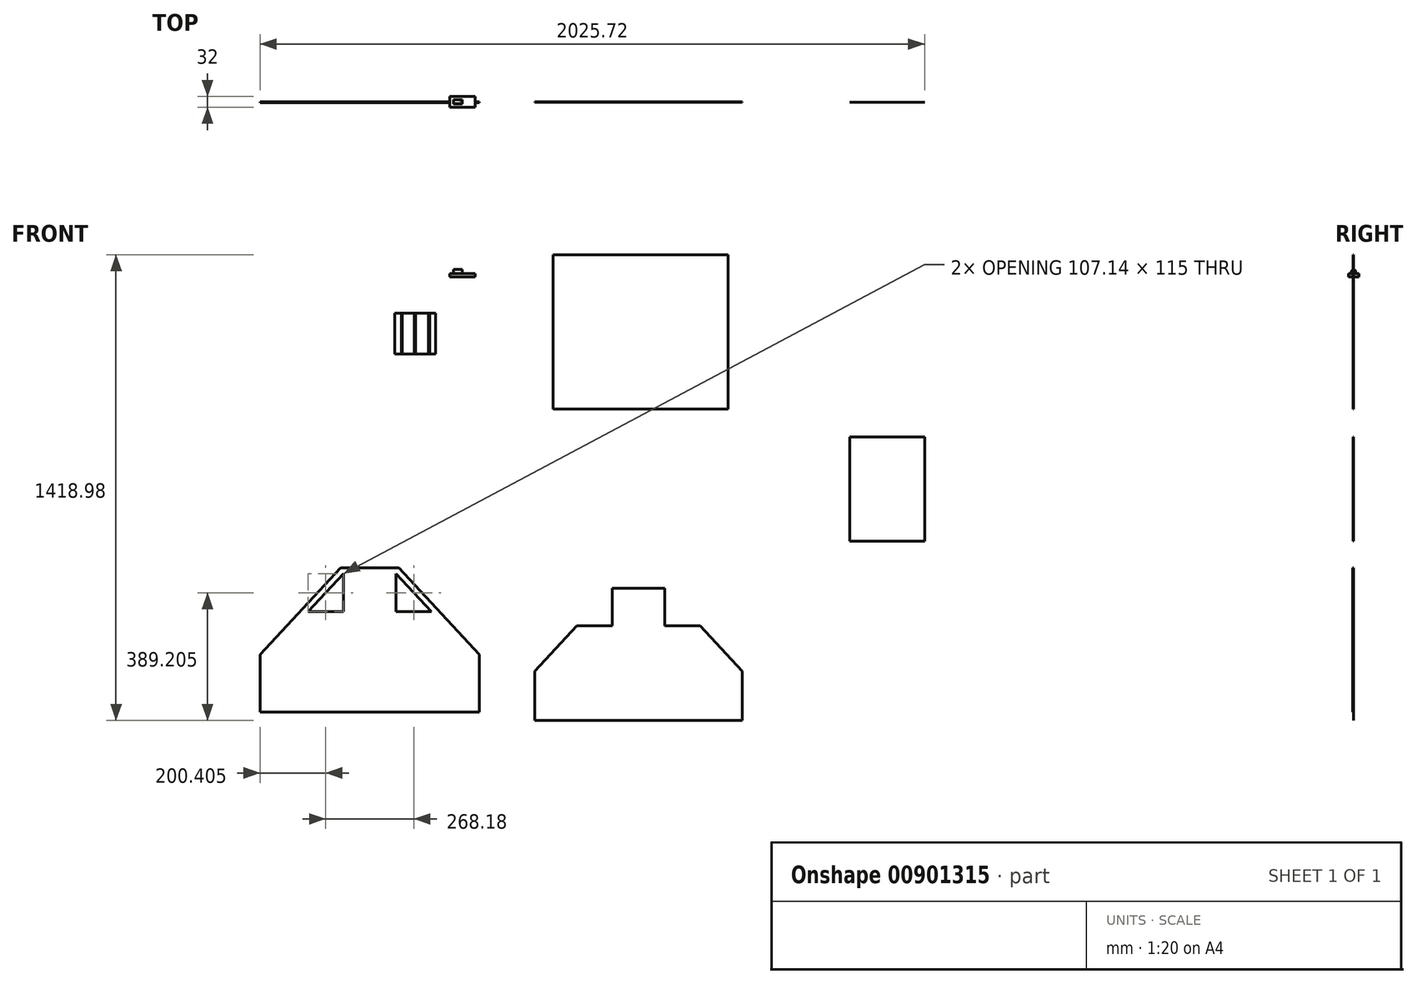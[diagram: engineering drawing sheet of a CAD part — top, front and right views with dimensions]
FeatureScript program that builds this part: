
annotation { "Feature Type Name" : "Feature", "Feature Type Description" : "" }
export const myFeature = defineFeature(function(context is Context, id is Id, definition is map)
    precondition{}
    {
        {
            var Q0;
            Q0=qCreatedBy(makeId("Front.planeOp"),FACE);
            var sketch = newSketch(context, id + "F0", { "sketchPlane" : qUnion([Q0])});
            skLineSegment(sketch, "E0.bottom", {"start": v(751.3, 665.77) * mm, "end": v(876.3, 665.77) * mm});
            skLineSegment(sketch, "E0.top", {"start": v(751.3, 540.77) * mm, "end": v(876.3, 540.77) * mm});
            skLineSegment(sketch, "E0.left", {"start": v(751.3, 665.77) * mm, "end": v(751.3, 540.77) * mm});
            skLineSegment(sketch, "E0.right", {"start": v(876.3, 665.77) * mm, "end": v(876.3, 540.77) * mm});
            skPoint(sketch, "E1.visualSharp", {"position": v(751.3, 665.77) * mm});
            skLineSegment(sketch, "E1.filletArc", {"start": v(751.3, 665.77) * mm, "end": v(751.3, 665.77) * mm});
            skPoint(sketch, "E2.visualSharp", {"position": v(876.3, 665.77) * mm});
            skLineSegment(sketch, "E2.filletArc", {"start": v(876.3, 665.77) * mm, "end": v(876.3, 665.77) * mm});
            skPoint(sketch, "E3.visualSharp", {"position": v(876.3, 540.77) * mm});
            skLineSegment(sketch, "E3.filletArc", {"start": v(876.3, 540.77) * mm, "end": v(876.3, 540.77) * mm});
            skPoint(sketch, "E4.visualSharp", {"position": v(751.3, 540.77) * mm});
            skLineSegment(sketch, "E4.filletArc", {"start": v(751.3, 540.77) * mm, "end": v(751.3, 540.77) * mm});
            skLineSegment(sketch, "E5.bottom", {"start": v(3038.85, 81858.35) * mm, "end": v(2869.38, 81858.35) * mm});
            skLineSegment(sketch, "E5.top", {"start": v(3038.85, 72650.5) * mm, "end": v(2869.38, 72650.5) * mm});
            skLineSegment(sketch, "E5.left", {"start": v(3038.85, 81858.35) * mm, "end": v(3038.85, 72650.5) * mm});
            skLineSegment(sketch, "E5.right", {"start": v(2869.38, 81858.35) * mm, "end": v(2869.38, 72650.5) * mm});
            skSolve(sketch);
        }
        {
            var Q0;
            Q0=makeQuery(id+"F0.imprint","IMPRINT",FACE,{"disambiguationData":[TD([[makeQuery(id+"F0.imprint","IMPRINT",EDGE,{"derivedFrom":sQuery(id+"F0.wireOp",EDGE,"E0.bottom")}),-1.0]])]});
            extrude(context, id + "F1", {"entities" : qUnion([Q0]), "depth" : 1 * mm, "offsetDistance" : 25 * mm});
        }
        {
            var Q0;
            Q0=makeQuery(id+"F1.opExtrude","CAP_FACE",FACE,{"disambiguationData":[OSD([sQuery(id+"F0.wireOp",EDGE,"E0.bottom"),sQuery(id+"F0.wireOp",EDGE,"E0.top"),sQuery(id+"F0.wireOp",EDGE,"E0.left"),sQuery(id+"F0.wireOp",EDGE,"E0.right"),sQuery(id+"F0.wireOp",EDGE,"E1.filletArc"),sQuery(id+"F0.wireOp",EDGE,"E2.filletArc"),sQuery(id+"F0.wireOp",EDGE,"E3.filletArc"),sQuery(id+"F0.wireOp",EDGE,"E4.filletArc")])],"isStart":false});
            var sketch = newSketch(context, id + "F2", { "sketchPlane" : qUnion([Q0])});
            skLineSegment(sketch, "E6.bottom", {"start": v(1062.52, 675.31) * mm, "end": v(1065.96, 675.31) * mm});
            skLineSegment(sketch, "E6.top", {"start": v(1062.52, 550.31) * mm, "end": v(1065.96, 550.31) * mm});
            skLineSegment(sketch, "E6.left", {"start": v(1062.52, 675.31) * mm, "end": v(1062.52, 550.31) * mm});
            skLineSegment(sketch, "E6.right", {"start": v(1065.96, 675.31) * mm, "end": v(1065.96, 550.31) * mm});
            skLineSegment(sketch, "E7.bottom", {"start": v(1040.06, 681.56) * mm, "end": v(1043.5, 681.56) * mm});
            skLineSegment(sketch, "E7.top", {"start": v(1040.06, 556.56) * mm, "end": v(1043.5, 556.56) * mm});
            skLineSegment(sketch, "E7.left", {"start": v(1040.06, 681.56) * mm, "end": v(1040.06, 556.56) * mm});
            skLineSegment(sketch, "E7.right", {"start": v(1043.5, 681.56) * mm, "end": v(1043.5, 556.56) * mm});
            skLineSegment(sketch, "E8.bottom", {"start": v(1006.11, 664.93) * mm, "end": v(1009.55, 664.93) * mm});
            skLineSegment(sketch, "E8.top", {"start": v(1006.11, 539.93) * mm, "end": v(1009.55, 539.93) * mm});
            skLineSegment(sketch, "E8.left", {"start": v(1006.11, 664.93) * mm, "end": v(1006.11, 539.93) * mm});
            skLineSegment(sketch, "E8.right", {"start": v(1009.55, 664.93) * mm, "end": v(1009.55, 539.93) * mm});
            skPoint(sketch, "E9.firstSnap0", {"position": v(1043.5, 619.06) * mm});
            skPoint(sketch, "E9.oppositeSnap0", {"position": v(1043.5, 619.06) * mm});
            skSolve(sketch);
        }
        {
            var Q0;
            Q0=makeQuery(id+"F2.imprint","IMPRINT",FACE,{"disambiguationData":[TD([[makeQuery(id+"F2.imprint","IMPRINT",EDGE,{"derivedFrom":sQuery(id+"F2.wireOp",EDGE,"E6.bottom")}),-1.0]])]});
            var Q1;
            Q1=makeQuery(id+"F2.imprint","IMPRINT",FACE,{"disambiguationData":[TD([[makeQuery(id+"F2.imprint","IMPRINT",EDGE,{"derivedFrom":sQuery(id+"F2.wireOp",EDGE,"E7.bottom")}),-1.0]])]});
            var Q2;
            Q2=makeQuery(id+"F2.imprint","IMPRINT",FACE,{"disambiguationData":[TD([[makeQuery(id+"F2.imprint","IMPRINT",EDGE,{"derivedFrom":sQuery(id+"F2.wireOp",EDGE,"E8.bottom")}),-1.0]])]});
            extrude(context, id + "F3", {"entities" : qUnion([Q0, Q1, Q2]), "depth" : 0.1 * mm, "offsetDistance" : 25 * mm});
        }
        {
            var Q0;
            Q0=makeQuery(id+"F3.opExtrude","SWEPT_BODY",BODY,{"disambiguationData":[OSD([sQuery(id+"F2.wireOp",EDGE,"E8.bottom"),sQuery(id+"F2.wireOp",EDGE,"E8.top"),sQuery(id+"F2.wireOp",EDGE,"E8.left"),sQuery(id+"F2.wireOp",EDGE,"E8.right")])]});
            transform(context, id + "F4", {"entities" : qUnion([Q0]), "transformType" : TransformType.TRANSLATION_3D, "dx" : -232.8 * mm, "dy" : 0 * mm, "dz" : 3.3 * mm, "makeCopy" : false});
        }
        {
            var Q0;
            Q0=makeQuery(id+"F3.opExtrude","SWEPT_BODY",BODY,{"disambiguationData":[OSD([sQuery(id+"F2.wireOp",EDGE,"E8.bottom"),sQuery(id+"F2.wireOp",EDGE,"E8.top"),sQuery(id+"F2.wireOp",EDGE,"E8.left"),sQuery(id+"F2.wireOp",EDGE,"E8.right")])]});
            transform(context, id + "F5", {"entities" : qUnion([Q0]), "transformType" : TransformType.TRANSLATION_3D, "dx" : 6E-4000 * mm, "dy" : 0 * mm, "dz" : 0 * mm, "makeCopy" : false});
        }
        {
            var Q0;
            Q0=makeQuery(id+"F3.opExtrude","SWEPT_BODY",BODY,{"disambiguationData":[OSD([sQuery(id+"F2.wireOp",EDGE,"E8.bottom"),sQuery(id+"F2.wireOp",EDGE,"E8.top"),sQuery(id+"F2.wireOp",EDGE,"E8.left"),sQuery(id+"F2.wireOp",EDGE,"E8.right")])]});
            var Q1;
            Q1=makeQuery(id+"F3.opExtrude","CAP_VERTEX",VERTEX,{"disambiguationData":[OSD([sQuery(id+"F2.wireOp",EDGE,"E8.top"),sQuery(id+"F2.wireOp",EDGE,"E8.left")])],"isStart":false});
            var Q2;
            Q2=makeQuery(id+"F1.opExtrude","CAP_EDGE",EDGE,{"disambiguationData":[OSD([sQuery(id+"F0.wireOp",EDGE,"E0.top")])],"isStart":false});
            transform(context, id + "F6", {"entities" : qUnion([Q0]), "transformType" : TransformType.TRANSLATION_ENTITY, "oppositeDirectionEntity" : false, "transformLine" : qUnion([Q1, Q2]), "makeCopy" : false});
        }
        {
            var Q0;
            Q0=makeQuery(id+"F3.opExtrude","SWEPT_BODY",BODY,{"disambiguationData":[OSD([sQuery(id+"F2.wireOp",EDGE,"E8.bottom"),sQuery(id+"F2.wireOp",EDGE,"E8.top"),sQuery(id+"F2.wireOp",EDGE,"E8.left"),sQuery(id+"F2.wireOp",EDGE,"E8.right")])]});
            var Q1;
            Q1=makeQuery(id+"F3.opExtrude","CAP_VERTEX",VERTEX,{"disambiguationData":[OSD([sQuery(id+"F2.wireOp",EDGE,"E8.bottom"),sQuery(id+"F2.wireOp",EDGE,"E8.right")])],"isStart":true});
            var Q2;
            Q2=makeQuery(id+"F1.opExtrude","CAP_VERTEX",VERTEX,{"disambiguationData":[OSD([sQuery(id+"F0.wireOp",EDGE,"E0.bottom"),sQuery(id+"F0.wireOp",EDGE,"E2.filletArc")])],"isStart":false});
            transform(context, id + "F7", {"entities" : qUnion([Q0]), "transformType" : TransformType.TRANSLATION_ENTITY, "oppositeDirectionEntity" : false, "transformLine" : qUnion([Q1, Q2]), "makeCopy" : false});
        }
        {
            var Q0;
            Q0=makeQuery(id+"F3.opExtrude","SWEPT_BODY",BODY,{"disambiguationData":[OSD([sQuery(id+"F2.wireOp",EDGE,"E7.bottom"),sQuery(id+"F2.wireOp",EDGE,"E7.top"),sQuery(id+"F2.wireOp",EDGE,"E7.left"),sQuery(id+"F2.wireOp",EDGE,"E7.right")])]});
            var Q1;
            Q1=sQuery(id+"F2.wireOp",VERTEX,"E7.bottom.start");
            var Q2;
            Q2=makeQuery(id+"F1.opExtrude","CAP_VERTEX",VERTEX,{"disambiguationData":[OSD([sQuery(id+"F0.wireOp",EDGE,"E0.bottom"),sQuery(id+"F0.wireOp",EDGE,"E1.filletArc")])],"isStart":false});
            transform(context, id + "F8", {"entities" : qUnion([Q0]), "transformType" : TransformType.TRANSLATION_ENTITY, "oppositeDirectionEntity" : false, "transformLine" : qUnion([Q1, Q2]), "makeCopy" : false});
        }
        {
            var Q0;
            Q0=sQuery(id+"F2.wireOp",EDGE,"E6.bottom");
            cPoint(context, id + "F9", {"entities" : qUnion([Q0]), "parameter" : 0.5});
        }
        {
            var Q0;
            Q0=makeQuery(id+"F1.opExtrude","CAP_EDGE",EDGE,{"disambiguationData":[OSD([sQuery(id+"F0.wireOp",EDGE,"E0.bottom")])],"isStart":false});
            cPoint(context, id + "F10", {"entities" : qUnion([Q0]), "parameter" : 0.5});
        }
        {
            var Q0;
            Q0=makeQuery(id+"F3.opExtrude","SWEPT_BODY",BODY,{"disambiguationData":[OSD([sQuery(id+"F2.wireOp",EDGE,"E6.bottom"),sQuery(id+"F2.wireOp",EDGE,"E6.top"),sQuery(id+"F2.wireOp",EDGE,"E6.left"),sQuery(id+"F2.wireOp",EDGE,"E6.right")])]});
            var Q1;
            Q1=qCreatedBy(id+"F9",VERTEX);
            var Q2;
            Q2=qCreatedBy(id+"F10",VERTEX);
            transform(context, id + "F11", {"entities" : qUnion([Q0]), "transformType" : TransformType.TRANSLATION_ENTITY, "oppositeDirectionEntity" : false, "transformLine" : qUnion([Q1, Q2]), "makeCopy" : false});
        }
        {
            var Q0;
            Q0=qCreatedBy(makeId("Front.planeOp"),FACE);
            var sketch = newSketch(context, id + "F12", { "sketchPlane" : qUnion([Q0])});
            skLineSegment(sketch, "E10.bottom", {"start": v(919.16, 786.05) * mm, "end": v(997.16, 786.05) * mm});
            skLineSegment(sketch, "E10.top", {"start": v(919.16, 776.05) * mm, "end": v(997.16, 776.05) * mm});
            skLineSegment(sketch, "E10.left", {"start": v(919.16, 786.05) * mm, "end": v(919.16, 776.05) * mm});
            skLineSegment(sketch, "E10.right", {"start": v(997.16, 786.05) * mm, "end": v(997.16, 776.05) * mm});
            skPoint(sketch, "E11.oppositeSnap0", {"position": v(958.16, 786.05) * mm});
            skLineSegment(sketch, "E11.bottom", {"start": v(997.16, 786.05) * mm, "end": v(958.16, 786.05) * mm});
            skLineSegment(sketch, "E11.top", {"start": v(997.16, 798.75) * mm, "end": v(958.16, 798.75) * mm});
            skLineSegment(sketch, "E11.left", {"start": v(997.16, 786.05) * mm, "end": v(997.16, 798.75) * mm});
            skLineSegment(sketch, "E11.right", {"start": v(958.16, 786.05) * mm, "end": v(958.16, 798.75) * mm});
            skLineSegment(sketch, "E12.bottom", {"start": v(958.16, 792.4) * mm, "end": v(930.77, 792.4) * mm});
            skLineSegment(sketch, "E12.top", {"start": v(958.16, 786.05) * mm, "end": v(930.77, 786.05) * mm});
            skLineSegment(sketch, "E12.left", {"start": v(958.16, 792.4) * mm, "end": v(958.16, 786.05) * mm});
            skLineSegment(sketch, "E12.right", {"start": v(930.77, 792.4) * mm, "end": v(930.77, 786.05) * mm});
            skSolve(sketch);
        }
        {
            var Q0;
            Q0=makeQuery(id+"F12.imprint","IMPRINT",FACE,{"disambiguationData":[TD([[makeQuery(id+"F12.imprint","IMPRINT",EDGE,{"derivedFrom":sQuery(id+"F12.wireOp",EDGE,"E11.bottom")}),-1.0]])]});
            var Q1;
            Q1=makeQuery(id+"F12.imprint","IMPRINT",FACE,{"disambiguationData":[TD([[makeQuery(id+"F12.imprint","IMPRINT",EDGE,{"derivedFrom":sQuery(id+"F12.wireOp",EDGE,"E10.bottom")}),-1.0]])]});
            extrude(context, id + "F13", {"entities" : qUnion([Q0, Q1]), "endBound" : BoundingType.SYMMETRIC, "depth" : 32 * mm, "offsetDistance" : 25 * mm});
        }
        {
            var Q0;
            Q0=makeQuery(id+"F12.imprint","IMPRINT",FACE,{"disambiguationData":[TD([[makeQuery(id+"F12.imprint","IMPRINT",EDGE,{"derivedFrom":sQuery(id+"F12.wireOp",EDGE,"E12.bottom")}),1.0]])]});
            var Q1;
            Q1=sQuery(id+"F12.wireOp",EDGE,"E12.bottom");
            revolve(context, id + "F14", {"surfaceOperationType" : NewSurfaceOperationType.NEW, "entities" : qUnion([Q0]), "axis" : qUnion([Q1]), "revolveType" : RevolveType.ONE_DIRECTION, "angle" : 360 * degree});
        }
        {
            var Q0;
            Q0=makeQuery(id+"F14.opRevolve","SWEPT_FACE",FACE,{"disambiguationData":[OSD([sQuery(id+"F12.wireOp",EDGE,"E12.right")])]});
            var sketch = newSketch(context, id + "F15", { "sketchPlane" : qUnion([Q0])});
            skCircle(sketch, "E13", {"center": v(0, 792.4) * mm, "radius": 7.66 * mm});
            skSolve(sketch);
        }
        {
            var Q0;
            Q0=makeQuery(id+"F15.imprint","IMPRINT",FACE,{"disambiguationData":[TD([[makeQuery(id+"F15.imprint","IMPRINT",EDGE,{"derivedFrom":sQuery(id+"F15.wireOp",EDGE,"E13")}),1.0]])]});
            extrude(context, id + "F16", {"entities" : qUnion([Q0]), "operationType" : NewBodyOperationType.REMOVE, "depth" : -20 * mm, "offsetDistance" : 25 * mm});
        }
        {
            var Q0;
            Q0=makeQuery(id+"F1.opExtrude","CAP_FACE",FACE,{"disambiguationData":[OSD([sQuery(id+"F0.wireOp",EDGE,"E0.bottom"),sQuery(id+"F0.wireOp",EDGE,"E0.top"),sQuery(id+"F0.wireOp",EDGE,"E0.left"),sQuery(id+"F0.wireOp",EDGE,"E0.right"),sQuery(id+"F0.wireOp",EDGE,"E1.filletArc"),sQuery(id+"F0.wireOp",EDGE,"E2.filletArc"),sQuery(id+"F0.wireOp",EDGE,"E3.filletArc"),sQuery(id+"F0.wireOp",EDGE,"E4.filletArc")])],"isStart":false});
            var sketch = newSketch(context, id + "F17", { "sketchPlane" : qUnion([Q0])});
            skLineSegment(sketch, "E14.bottom", {"start": v(1234.72, 843.78) * mm, "end": v(1768.12, 843.78) * mm});
            skLineSegment(sketch, "E14.top", {"start": v(1234.72, 373.88) * mm, "end": v(1768.12, 373.88) * mm});
            skLineSegment(sketch, "E14.left", {"start": v(1234.72, 843.78) * mm, "end": v(1234.72, 373.88) * mm});
            skLineSegment(sketch, "E14.right", {"start": v(1768.12, 843.78) * mm, "end": v(1768.12, 373.88) * mm});
            skSolve(sketch);
        }
        {
            var Q0;
            Q0=makeQuery(id+"F17.imprint","IMPRINT",FACE,{"disambiguationData":[TD([[makeQuery(id+"F17.imprint","IMPRINT",EDGE,{"derivedFrom":sQuery(id+"F17.wireOp",EDGE,"E14.bottom")}),-1.0]])]});
            extrude(context, id + "F18", {"entities" : qUnion([Q0]), "endBound" : BoundingType.SYMMETRIC, "depth" : 1 * mm, "offsetDistance" : 25.4 * mm});
        }
        {
            var Q0;
            Q0=makeQuery(id+"F18.opExtrude","CAP_FACE",FACE,{"disambiguationData":[OSD([sQuery(id+"F17.wireOp",EDGE,"E14.bottom"),sQuery(id+"F17.wireOp",EDGE,"E14.top"),sQuery(id+"F17.wireOp",EDGE,"E14.left"),sQuery(id+"F17.wireOp",EDGE,"E14.right")])],"isStart":false});
            var sketch = newSketch(context, id + "F19", { "sketchPlane" : qUnion([Q0])});
            skLineSegment(sketch, "E15.bottom", {"start": v(2138.3, 288.85) * mm, "end": v(2366.9, 288.85) * mm});
            skLineSegment(sketch, "E15.top", {"start": v(2138.3, -28.65) * mm, "end": v(2366.9, -28.65) * mm});
            skLineSegment(sketch, "E15.left", {"start": v(2138.3, 288.85) * mm, "end": v(2138.3, -28.65) * mm});
            skLineSegment(sketch, "E15.right", {"start": v(2366.9, 288.85) * mm, "end": v(2366.9, -28.65) * mm});
            skSolve(sketch);
        }
        {
            var Q0;
            Q0=makeQuery(id+"F19.imprint","IMPRINT",FACE,{"disambiguationData":[TD([[makeQuery(id+"F19.imprint","IMPRINT",EDGE,{"derivedFrom":sQuery(id+"F19.wireOp",EDGE,"E15.bottom")}),-1.0]])]});
            extrude(context, id + "F20", {"entities" : qUnion([Q0]), "endBound" : BoundingType.SYMMETRIC, "depth" : 1 * mm, "offsetDistance" : 25.4 * mm});
        }
        {
            var Q0;
            Q0=makeQuery(id+"F3.opExtrude","SWEPT_BODY",BODY,{"disambiguationData":[OSD([sQuery(id+"F2.wireOp",EDGE,"E7.bottom"),sQuery(id+"F2.wireOp",EDGE,"E7.top"),sQuery(id+"F2.wireOp",EDGE,"E7.left"),sQuery(id+"F2.wireOp",EDGE,"E7.right")])]});
            transform(context, id + "F21", {"entities" : qUnion([Q0]), "transformType" : TransformType.TRANSLATION_3D, "dx" : 21.1 * mm, "dy" : 0 * mm, "dz" : 0 * mm, "makeCopy" : false});
        }
        {
            var Q0;
            Q0=makeQuery(id+"F3.opExtrude","SWEPT_BODY",BODY,{"disambiguationData":[OSD([sQuery(id+"F2.wireOp",EDGE,"E8.bottom"),sQuery(id+"F2.wireOp",EDGE,"E8.top"),sQuery(id+"F2.wireOp",EDGE,"E8.left"),sQuery(id+"F2.wireOp",EDGE,"E8.right")])]});
            transform(context, id + "F22", {"entities" : qUnion([Q0]), "transformType" : TransformType.TRANSLATION_3D, "dx" : 107.2 * mm, "dy" : 0 * mm, "dz" : 0 * mm, "makeCopy" : false});
        }
        {
            var Q0;
            Q0=makeQuery(id+"F3.opExtrude","SWEPT_BODY",BODY,{"disambiguationData":[OSD([sQuery(id+"F2.wireOp",EDGE,"E8.bottom"),sQuery(id+"F2.wireOp",EDGE,"E8.top"),sQuery(id+"F2.wireOp",EDGE,"E8.left"),sQuery(id+"F2.wireOp",EDGE,"E8.right")])]});
            transform(context, id + "F23", {"entities" : qUnion([Q0]), "transformType" : TransformType.TRANSLATION_3D, "dx" : -.460 * mm, "dy" : 0 * mm, "dz" : 0 * mm, "makeCopy" : false});
        }
        {
            var Q0;
            Q0=makeQuery(id+"F3.opExtrude","SWEPT_BODY",BODY,{"disambiguationData":[OSD([sQuery(id+"F2.wireOp",EDGE,"E7.bottom"),sQuery(id+"F2.wireOp",EDGE,"E7.top"),sQuery(id+"F2.wireOp",EDGE,"E7.left"),sQuery(id+"F2.wireOp",EDGE,"E7.right")])]});
            transform(context, id + "F24", {"entities" : qUnion([Q0]), "transformType" : TransformType.TRANSLATION_3D, "dx" : .840 * mm, "dy" : 0 * mm, "dz" : 0 * mm, "makeCopy" : false});
        }
        {
            var Q0;
            Q0=makeQuery(id+"F3.opExtrude","SWEPT_BODY",BODY,{"disambiguationData":[OSD([sQuery(id+"F2.wireOp",EDGE,"E7.bottom"),sQuery(id+"F2.wireOp",EDGE,"E7.top"),sQuery(id+"F2.wireOp",EDGE,"E7.left"),sQuery(id+"F2.wireOp",EDGE,"E7.right")])]});
            transform(context, id + "F25", {"entities" : qUnion([Q0]), "transformType" : TransformType.TRANSLATION_3D, "dx" : -1.68 * mm, "dy" : 0 * mm, "dz" : 0 * mm, "makeCopy" : false});
        }
        {
            var Q0;
            Q0=qCreatedBy(makeId("Front.planeOp"),FACE);
            var sketch = newSketch(context, id + "F26", { "sketchPlane" : qUnion([Q0])});
            skLineSegment(sketch, "E16.top", {"start": v(341.18, -549.5) * mm, "end": v(1010.18, -549.5) * mm});
            skLineSegment(sketch, "E17.bottom", {"start": v(764.03, -110.5) * mm, "end": v(587.33, -110.5) * mm});
            skLineSegment(sketch, "E17.top", {"start": v(764.03, -110.5) * mm, "end": v(587.33, -110.5) * mm});
            skLineSegment(sketch, "E17.left", {"start": v(764.03, -110.5) * mm, "end": v(764.03, -110.5) * mm});
            skLineSegment(sketch, "E17.right", {"start": v(587.33, -110.5) * mm, "end": v(587.33, -110.5) * mm});
            skPoint(sketch, "E17.middle", {"position": v(675.68, -110.5) * mm});
            skLineSegment(sketch, "E18", {"start": v(341.18, -549.5) * mm, "end": v(341.18, -374.7) * mm});
            skLineSegment(sketch, "E19", {"start": v(1010.18, -549.5) * mm, "end": v(1010.18, -374.7) * mm});
            skLineSegment(sketch, "E20", {"start": v(341.18, -374.7) * mm, "end": v(587.33, -110.5) * mm});
            skLineSegment(sketch, "E21", {"start": v(1010.18, -374.7) * mm, "end": v(764.03, -110.5) * mm});
            skLineSegment(sketch, "E22", {"start": v(756.2, -128.5) * mm, "end": v(756.2, -243.5) * mm});
            skLineSegment(sketch, "E23", {"start": v(756.2, -243.5) * mm, "end": v(863.34, -243.5) * mm});
            skLineSegment(sketch, "E24", {"start": v(595.16, -128.5) * mm, "end": v(595.16, -243.5) * mm});
            skLineSegment(sketch, "E25", {"start": v(595.16, -243.5) * mm, "end": v(488.01, -243.5) * mm});
            skLineSegment(sketch, "E26.0", {"start": v(1178.34, -575.2) * mm, "end": v(1178.34, -425.49) * mm});
            skLineSegment(sketch, "E26.1", {"start": v(1575.36, -172.2) * mm, "end": v(1414.32, -172.2) * mm});
            skLineSegment(sketch, "E26.4", {"start": v(1811.34, -575.2) * mm, "end": v(1811.34, -425.49) * mm});
            skLineSegment(sketch, "E26.5", {"start": v(1178.34, -575.2) * mm, "end": v(1811.34, -575.2) * mm});
            skLineSegment(sketch, "E27", {"start": v(1575.36, -172.2) * mm, "end": v(1575.36, -287.2) * mm});
            skLineSegment(sketch, "E28", {"start": v(1575.36, -287.2) * mm, "end": v(1682.5, -287.2) * mm});
            skLineSegment(sketch, "E29", {"start": v(1414.32, -172.2) * mm, "end": v(1414.32, -287.2) * mm});
            skLineSegment(sketch, "E30", {"start": v(1414.32, -287.2) * mm, "end": v(1307.18, -287.2) * mm});
            skLineSegment(sketch, "E31", {"start": v(1178.34, -425.49) * mm, "end": v(1307.18, -287.2) * mm});
            skLineSegment(sketch, "E32", {"start": v(1682.5, -287.2) * mm, "end": v(1811.34, -425.49) * mm});
            skLineSegment(sketch, "E33", {"start": v(488.01, -243.5) * mm, "end": v(595.16, -128.5) * mm});
            skLineSegment(sketch, "E34", {"start": v(756.2, -128.5) * mm, "end": v(863.34, -243.5) * mm});
            skSolve(sketch);
        }
        {
            var Q0;
            Q0=makeQuery(id+"F26.imprint","IMPRINT",FACE,{"disambiguationData":[TD([[makeQuery(id+"F26.imprint","IMPRINT",EDGE,{"derivedFrom":sQuery(id+"F26.wireOp",EDGE,"E16.top")}),1.0]])]});
            extrude(context, id + "F27", {"entities" : qUnion([Q0]), "depth" : 3 * mm, "offsetDistance" : 25 * mm});
        }
        {
            var Q0;
            Q0 = qSketchRegion(id + "F26", true);
            extrude(context, id + "F28", {"entities" : qUnion([Q0]), "operationType" : NewBodyOperationType.ADD, "depth" : 1 * mm, "offsetDistance" : 25 * mm});
        }
    });
